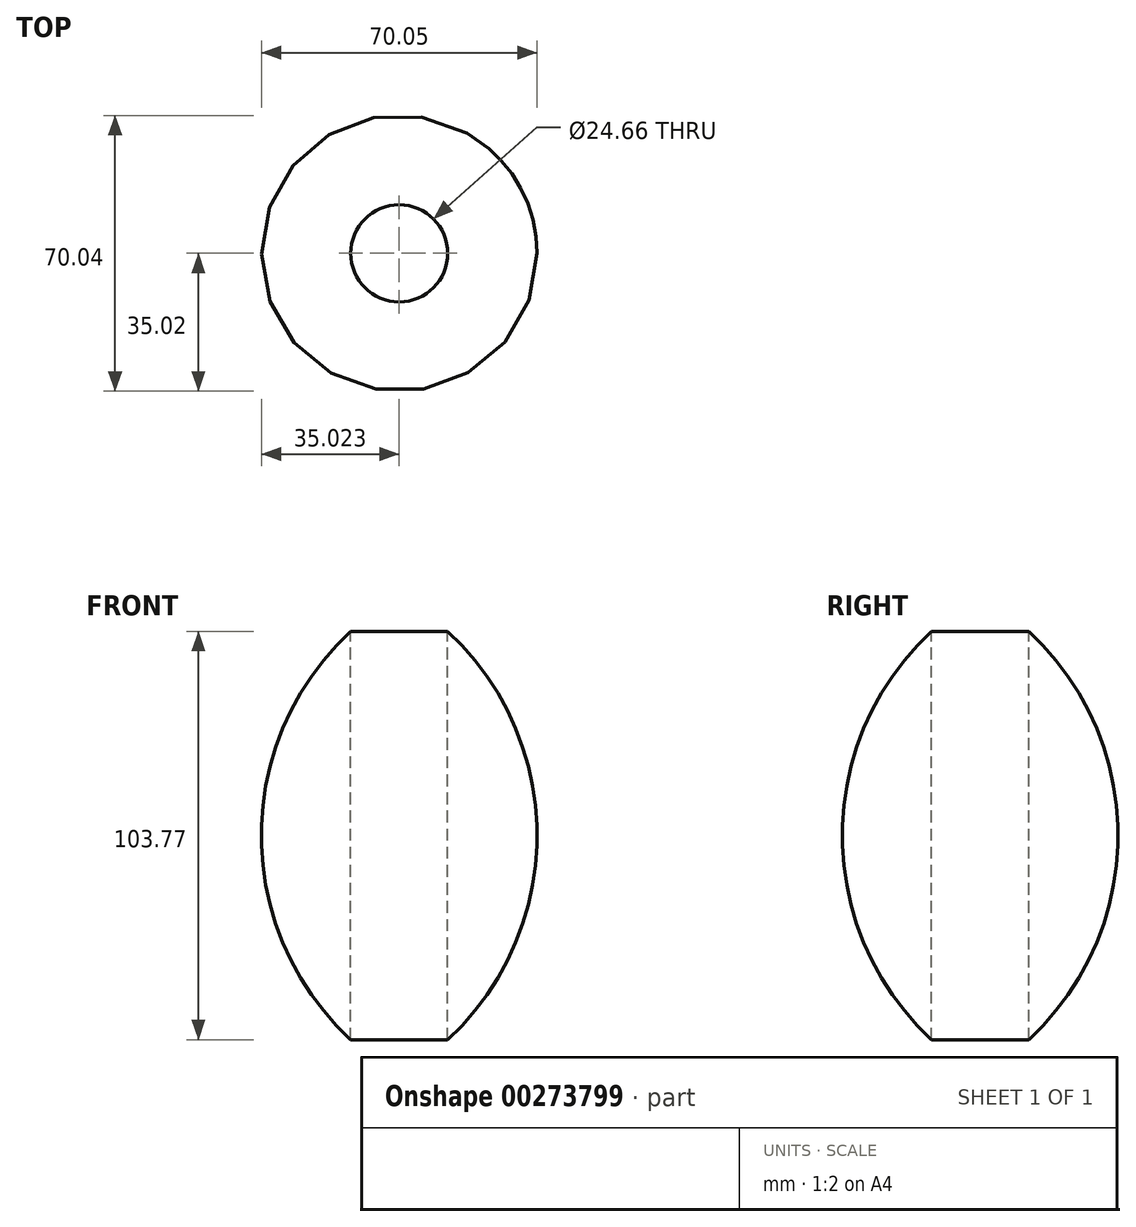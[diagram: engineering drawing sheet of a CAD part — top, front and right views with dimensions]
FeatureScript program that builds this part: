
annotation { "Feature Type Name" : "Feature", "Feature Type Description" : "" }
export const myFeature = defineFeature(function(context is Context, id is Id, definition is map)
    precondition{}
    {
        {
            var Q0;
            Q0=qCreatedBy(makeId("Front.planeOp"),FACE);
            var sketch = newSketch(context, id + "F0", { "sketchPlane" : qUnion([Q0])});
            skLineSegment(sketch, "E0", {"start": v(-21.66, 64.67) * mm, "end": v(-21.66, -41.8) * mm});
            skLineSegment(sketch, "E1", {"start": v(-9.32, 64.67) * mm, "end": v(-9.32, -39.1) * mm});
            skArc(sketch, "E2", {"start": v(-9.32, -39.1) * mm, "mid": v(13.37, 12.78) * mm, "end": v(-9.32, 64.67) * mm});
            skSolve(sketch);
        }
        {
            var Q0;
            Q0=makeQuery(id+"F0.imprint","IMPRINT",FACE,{"disambiguationData":[TD([[makeQuery(id+"F0.imprint","IMPRINT",EDGE,{"derivedFrom":sQuery(id+"F0.wireOp",EDGE,"E1")}),1.0]])]});
            var Q1;
            Q1=sQuery(id+"F0.wireOp",EDGE,"E0");
            revolve(context, id + "F1", {"entities" : qUnion([Q0]), "axis" : qUnion([Q1]), "revolveType" : RevolveType.FULL});
        }
    });
